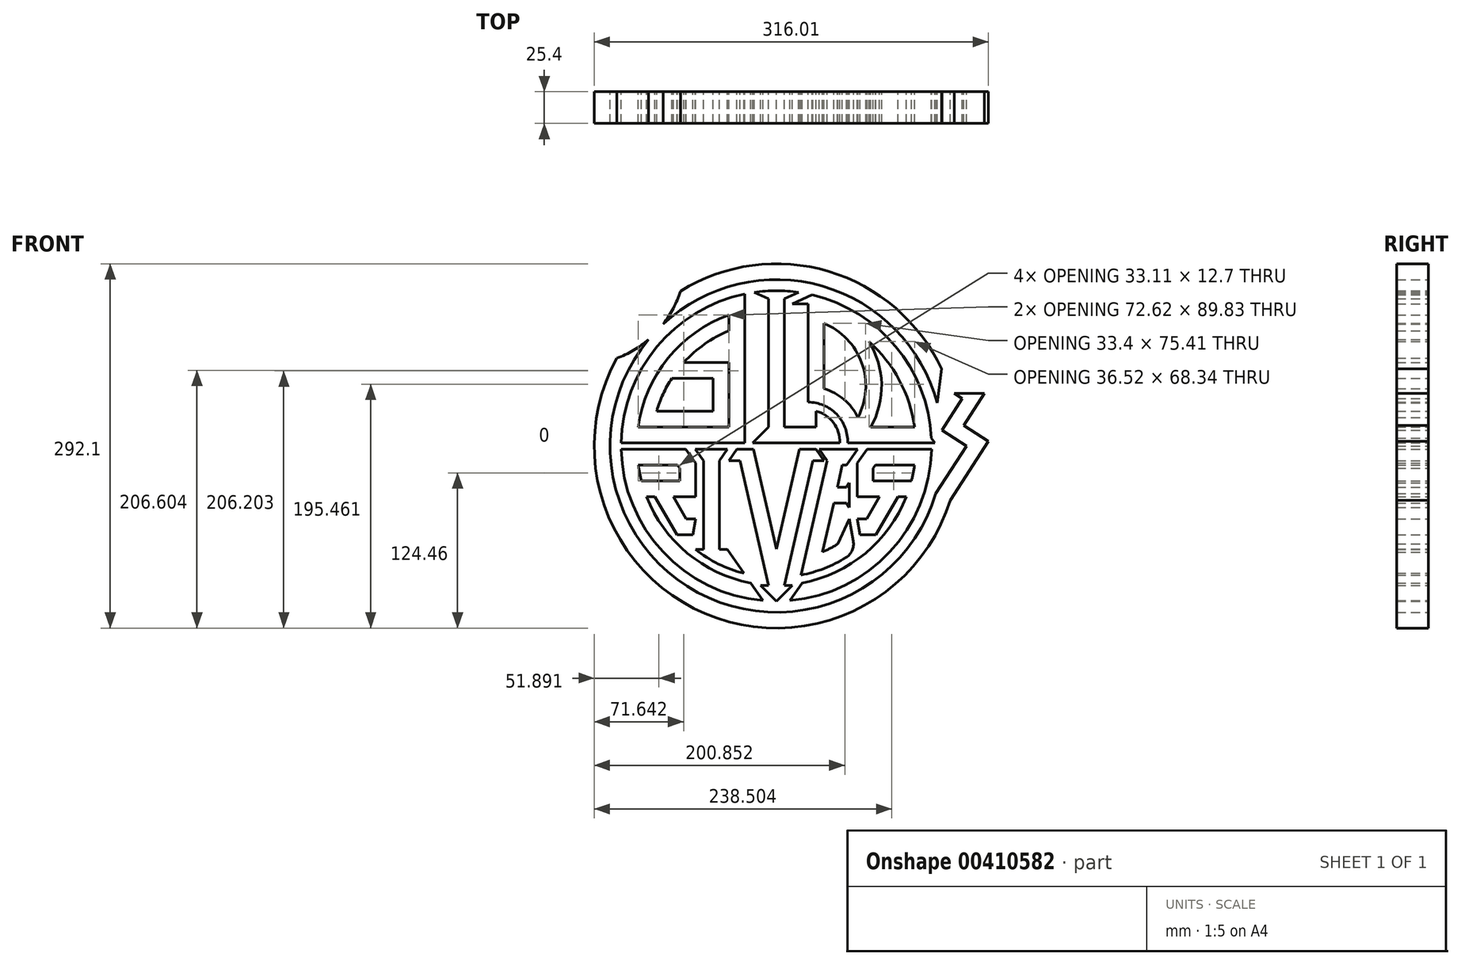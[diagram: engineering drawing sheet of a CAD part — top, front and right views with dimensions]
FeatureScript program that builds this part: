
annotation { "Feature Type Name" : "Feature", "Feature Type Description" : "" }
export const myFeature = defineFeature(function(context is Context, id is Id, definition is map)
    precondition{}
    {
        {
            var Q0;
            Q0=qCreatedBy(makeId("Front.planeOp"),FACE);
            var sketch = newSketch(context, id + "F0", { "sketchPlane" : qUnion([Q0])});
            skCircle(sketch, "E0", {"center": v(0, 0) * mm, "radius": 127 * mm});
            skLineSegment(sketch, "E1", {"start": v(-127, 0) * mm, "end": v(127, 0) * mm, "construction": true});
            skLineSegment(sketch, "E2", {"start": v(0, 127) * mm, "end": v(0, -127) * mm, "construction": true});
            skSolve(sketch);
        }
        {
            var Q0;
            Q0=qCreatedBy(makeId("Front.planeOp"),FACE);
            var sketch = newSketch(context, id + "F1", { "sketchPlane" : qUnion([Q0])});
            skArc(sketch, "E3", {"start": v(-124.43, 2.54) * mm, "mid": v(-95.76, 79.5) * mm, "end": v(-25.4, 121.84) * mm});
            skPoint(sketch, "E4.visualSharp", {"position": v(-124.46, 0) * mm});
            skPoint(sketch, "E5.visualSharp", {"position": v(0, 10.87) * mm});
            skPoint(sketch, "E6.visualSharp", {"position": v(-44.61, 116.2) * mm});
            skLineSegment(sketch, "E7", {"start": v(-25.4, 121.84) * mm, "end": v(-25.4, 2.54) * mm});
            skLineSegment(sketch, "E8", {"start": v(-25.4, 2.54) * mm, "end": v(-124.43, 2.54) * mm});
            skLineSegment(sketch, "E9", {"start": v(-17.78, 123.18) * mm, "end": v(-17.78, 123.18) * mm});
            skLineSegment(sketch, "E10", {"start": v(17.78, 123.18) * mm, "end": v(17.78, 123.18) * mm});
            skArc(sketch, "E11", {"start": v(17.78, 123.18) * mm, "mid": v(0, 124.46) * mm, "end": v(-17.78, 123.18) * mm});
            skPoint(sketch, "E12", {"position": v(0, 124.46) * mm});
            skLineSegment(sketch, "E13", {"start": v(-17.78, 123.18) * mm, "end": v(-6.35, 118.11) * mm});
            skLineSegment(sketch, "E14", {"start": v(-6.35, 118.11) * mm, "end": v(-6.35, 15.24) * mm});
            skLineSegment(sketch, "E15", {"start": v(17.78, 123.18) * mm, "end": v(6.35, 118.11) * mm});
            skLineSegment(sketch, "E16", {"start": v(6.35, 118.11) * mm, "end": v(6.35, 15.24) * mm});
            skLineSegment(sketch, "E17", {"start": v(-6.35, 15.24) * mm, "end": v(-19.05, 2.54) * mm});
            skLineSegment(sketch, "E18", {"start": v(-19.05, 2.54) * mm, "end": v(50.8, 2.54) * mm});
            skLineSegment(sketch, "E19", {"start": v(6.35, 15.24) * mm, "end": v(31.75, 15.24) * mm});
            skLineSegment(sketch, "E20", {"start": v(31.75, 15.24) * mm, "end": v(31.75, 27.94) * mm});
            skArc(sketch, "E21", {"start": v(50.8, 2.54) * mm, "mid": v(45.73, 18.58) * mm, "end": v(31.75, 27.94) * mm});
            skArc(sketch, "E22", {"start": v(-38.1, 105.07) * mm, "mid": v(-86.91, 70.26) * mm, "end": v(-110.72, 15.24) * mm});
            skLineSegment(sketch, "E23", {"start": v(-110.72, 15.24) * mm, "end": v(-38.1, 15.24) * mm});
            skLineSegment(sketch, "E24", {"start": v(-38.1, 15.24) * mm, "end": v(-38.1, 66.97) * mm});
            skLineSegment(sketch, "E25", {"start": v(-38.1, 66.97) * mm, "end": v(-74.15, 66.97) * mm});
            skLineSegment(sketch, "E26", {"start": v(-38.1, 105.07) * mm, "end": v(-38.1, 92.37) * mm});
            skArc(sketch, "E27", {"start": v(-38.1, 92.37) * mm, "mid": v(-57.55, 81.68) * mm, "end": v(-74.15, 66.97) * mm});
            skLineSegment(sketch, "E28.bottom", {"start": v(-50.8, 54.27) * mm, "end": v(-83.9, 54.27) * mm});
            skLineSegment(sketch, "E28.top", {"start": v(-50.8, 27.94) * mm, "end": v(-95.93, 27.94) * mm});
            skLineSegment(sketch, "E28.left", {"start": v(-50.8, 54.27) * mm, "end": v(-50.8, 27.94) * mm});
            skArc(sketch, "E29", {"start": v(-83.9, 54.27) * mm, "mid": v(-90.87, 41.54) * mm, "end": v(-95.93, 27.94) * mm});
            skSolve(sketch);
        }
        {
            var Q0;
            Q0=qCreatedBy(makeId("Front.planeOp"),FACE);
            var sketch = newSketch(context, id + "F2", { "sketchPlane" : qUnion([Q0])});
            skLineSegment(sketch, "E30", {"start": v(57.15, 2.54) * mm, "end": v(126.97, 2.54) * mm});
            skPoint(sketch, "E31.start.orphan", {"position": v(50.8, 46.41) * mm});
            skArc(sketch, "E32", {"start": v(25.4, 35.1) * mm, "mid": v(48.14, 25.51) * mm, "end": v(57.15, 2.54) * mm});
            skLineSegment(sketch, "E33", {"start": v(25.4, 35.1) * mm, "end": v(25.4, 113.98) * mm});
            skLineSegment(sketch, "E34", {"start": v(25.4, 113.98) * mm, "end": v(12.7, 113.98) * mm});
            skLineSegment(sketch, "E35", {"start": v(28.73, 121.1) * mm, "end": v(12.7, 113.98) * mm});
            skLineSegment(sketch, "E36", {"start": v(124.3, 6.35) * mm, "end": v(126.97, 2.54) * mm});
            skArc(sketch, "E37", {"start": v(28.73, 121.1) * mm, "mid": v(95.64, 79.65) * mm, "end": v(124.3, 6.35) * mm});
            skLineSegment(sketch, "E38", {"start": v(38.1, 105.07) * mm, "end": v(38.1, 45.94) * mm});
            skLineSegment(sketch, "E39", {"start": v(68.24, 15.24) * mm, "end": v(110.72, 15.24) * mm});
            skArc(sketch, "E40", {"start": v(38.1, 45.94) * mm, "mid": v(57.13, 34.48) * mm, "end": v(68.24, 15.24) * mm});
            skArc(sketch, "E41", {"start": v(38.1, 105.07) * mm, "mid": v(86.91, 70.26) * mm, "end": v(110.72, 15.24) * mm});
            skPoint(sketch, "E42.start.orphan", {"position": v(86.91, 70.26) * mm});
            skArc(sketch, "E43", {"start": v(68.24, 15.24) * mm, "mid": v(74.84, 67.42) * mm, "end": v(38.1, 105.07) * mm, "construction": true});
            skArc(sketch, "E44.0", {"start": v(75.66, 15.24) * mm, "mid": v(84.32, 49.61) * mm, "end": v(74.2, 83.58) * mm});
            skArc(sketch, "E45.0", {"start": v(65.35, 22.85) * mm, "mid": v(68.41, 66.58) * mm, "end": v(38.1, 98.26) * mm});
            skSolve(sketch);
        }
        {
            var Q0;
            Q0 = qSketchRegion(id + "F1", true);
            extrude(context, id + "F3", {"entities" : qUnion([Q0]), "depth" : 25.4 * mm});
        }
        {
            var Q0;
            Q0=qCreatedBy(makeId("Front.planeOp"),FACE);
            var sketch = newSketch(context, id + "F4", { "sketchPlane" : qUnion([Q0])});
            skLineSegment(sketch, "E46.0", {"start": v(-50.8, 54.27) * mm, "end": v(-83.9, 54.27) * mm});
            skPoint(sketch, "E47.0", {"position": v(-50.8, 27.94) * mm});
            skLineSegment(sketch, "E48.0", {"start": v(-50.8, 54.27) * mm, "end": v(-50.8, 27.94) * mm});
            skLineSegment(sketch, "E49.0", {"start": v(-50.8, 27.94) * mm, "end": v(-95.93, 27.94) * mm});
            skArc(sketch, "E50.0", {"start": v(-83.9, 54.27) * mm, "mid": v(-90.87, 41.54) * mm, "end": v(-95.93, 27.94) * mm});
            skSolve(sketch);
        }
        {
            var Q0;
            Q0 = qSketchRegion(id + "F4", true);
            extrude(context, id + "F5", {"entities" : qUnion([Q0]), "depth" : 25.4 * mm});
        }
        {
            var Q0;
            Q0 = qSketchRegion(id + "F2", true);
            extrude(context, id + "F6", {"entities" : qUnion([Q0]), "depth" : 25.4 * mm});
        }
        {
            var Q0;
            Q0=qCreatedBy(makeId("Front.planeOp"),FACE);
            var sketch = newSketch(context, id + "F7", { "sketchPlane" : qUnion([Q0])});
            skArc(sketch, "E51.0", {"start": v(65.35, 22.85) * mm, "mid": v(68.41, 66.58) * mm, "end": v(38.1, 98.26) * mm});
            skArc(sketch, "E52.0", {"start": v(75.66, 15.24) * mm, "mid": v(84.32, 49.61) * mm, "end": v(74.2, 83.58) * mm});
            skArc(sketch, "E53.0", {"start": v(38.1, 105.07) * mm, "mid": v(57.16, 96.03) * mm, "end": v(74.2, 83.58) * mm});
            skArc(sketch, "E54.0", {"start": v(65.35, 22.85) * mm, "mid": v(66.97, 19.11) * mm, "end": v(68.24, 15.24) * mm});
            skLineSegment(sketch, "E55.0", {"start": v(68.24, 15.24) * mm, "end": v(75.66, 15.24) * mm});
            skLineSegment(sketch, "E56.0", {"start": v(38.1, 105.07) * mm, "end": v(38.1, 98.26) * mm});
            skPoint(sketch, "E57.orphan", {"position": v(38.1, 45.94) * mm});
            skPoint(sketch, "E58.orphan", {"position": v(110.72, 15.24) * mm});
            skSolve(sketch);
        }
        {
            var Q0;
            Q0 = qSketchRegion(id + "F7", true);
            extrude(context, id + "F8", {"entities" : qUnion([Q0]), "operationType" : NewBodyOperationType.ADD, "depth" : 25.4 * mm});
        }
        {
            var Q0;
            Q0=qCreatedBy(makeId("Front.planeOp"),FACE);
            var sketch = newSketch(context, id + "F9", { "sketchPlane" : qUnion([Q0])});
            skLineSegment(sketch, "E59", {"start": v(-31.64, -2.54) * mm, "end": v(-38.1, -11.76) * mm});
            skLineSegment(sketch, "E60", {"start": v(-38.1, -11.76) * mm, "end": v(-29.21, -11.76) * mm});
            skLineSegment(sketch, "E61", {"start": v(-31.64, -2.54) * mm, "end": v(-18.3, -2.54) * mm});
            skLineSegment(sketch, "E62", {"start": v(-18.3, -2.54) * mm, "end": v(0, -82.55) * mm});
            skPoint(sketch, "E63.end.orphan", {"position": v(0, -100.04) * mm});
            skLineSegment(sketch, "E64", {"start": v(-29.21, -11.76) * mm, "end": v(-6.35, -111.76) * mm});
            skLineSegment(sketch, "E65", {"start": v(-6.35, -111.76) * mm, "end": v(-12.7, -111.76) * mm});
            skLineSegment(sketch, "E66", {"start": v(-12.7, -111.76) * mm, "end": v(0, -124.46) * mm});
            skLineSegment(sketch, "E67.MirrorCS", {"start": v(12.7, -111.76) * mm, "end": v(0, -124.46) * mm});
            skLineSegment(sketch, "E68.MirrorCS", {"start": v(29.21, -11.76) * mm, "end": v(6.35, -111.76) * mm});
            skLineSegment(sketch, "E69.MirrorCS", {"start": v(6.35, -111.76) * mm, "end": v(12.7, -111.76) * mm});
            skLineSegment(sketch, "E70.MirrorCS", {"start": v(18.3, -2.54) * mm, "end": v(0, -82.55) * mm});
            skLineSegment(sketch, "E71.MirrorCS", {"start": v(31.64, -2.54) * mm, "end": v(38.1, -11.76) * mm});
            skLineSegment(sketch, "E72.MirrorCS", {"start": v(38.1, -11.76) * mm, "end": v(29.21, -11.76) * mm});
            skLineSegment(sketch, "E73", {"start": v(18.3, -2.54) * mm, "end": v(31.64, -2.54) * mm});
            skLineSegment(sketch, "E74", {"start": v(-65.01, -2.54) * mm, "end": v(-39.4, -2.54) * mm});
            skLineSegment(sketch, "E75", {"start": v(-39.4, -2.54) * mm, "end": v(-45.85, -11.76) * mm});
            skLineSegment(sketch, "E76", {"start": v(-45.85, -11.76) * mm, "end": v(-45.85, -83.06) * mm});
            skLineSegment(sketch, "E77", {"start": v(-65.01, -2.54) * mm, "end": v(-58.55, -11.76) * mm});
            skLineSegment(sketch, "E78", {"start": v(-58.55, -11.76) * mm, "end": v(-58.55, -83.06) * mm});
            skLineSegment(sketch, "E79", {"start": v(-26.16, -102.11) * mm, "end": v(-39.5, -83.06) * mm});
            skLineSegment(sketch, "E80", {"start": v(-45.85, -83.06) * mm, "end": v(-39.5, -83.06) * mm});
            skLineSegment(sketch, "E81", {"start": v(-58.55, -83.06) * mm, "end": v(-64.9, -83.06) * mm});
            skArc(sketch, "E82", {"start": v(-64.9, -83.06) * mm, "mid": v(-46.52, -94.6) * mm, "end": v(-26.16, -102.11) * mm});
            skLineSegment(sketch, "E83", {"start": v(-124.43, -2.54) * mm, "end": v(-72.76, -2.54) * mm});
            skLineSegment(sketch, "E84", {"start": v(-72.76, -2.54) * mm, "end": v(-64.9, -13.77) * mm});
            skLineSegment(sketch, "E85", {"start": v(-64.9, -13.77) * mm, "end": v(-64.9, -40.64) * mm});
            skLineSegment(sketch, "E86", {"start": v(-64.9, -40.64) * mm, "end": v(-82.68, -40.64) * mm});
            skLineSegment(sketch, "E87", {"start": v(-82.68, -40.64) * mm, "end": v(-72.42, -58.42) * mm});
            skLineSegment(sketch, "E88", {"start": v(-72.42, -58.42) * mm, "end": v(-64.9, -58.42) * mm});
            skLineSegment(sketch, "E89", {"start": v(-64.9, -58.42) * mm, "end": v(-67.14, -71.12) * mm});
            skLineSegment(sketch, "E90", {"start": v(-67.14, -71.12) * mm, "end": v(-79.75, -71.12) * mm});
            skLineSegment(sketch, "E91", {"start": v(-79.75, -71.12) * mm, "end": v(-97.35, -40.64) * mm});
            skArc(sketch, "E92", {"start": v(-124.43, -2.54) * mm, "mid": v(-90.9, -85.02) * mm, "end": v(-10.84, -123.99) * mm});
            skArc(sketch, "E93", {"start": v(-104.1, -40.64) * mm, "mid": v(-71.38, -86) * mm, "end": v(-20.77, -109.81) * mm});
            skLineSegment(sketch, "E94", {"start": v(-97.35, -40.64) * mm, "end": v(-104.1, -40.64) * mm});
            skLineSegment(sketch, "E95", {"start": v(-20.77, -109.81) * mm, "end": v(-10.84, -123.99) * mm});
            skLineSegment(sketch, "E96", {"start": v(-20.77, -109.81) * mm, "end": v(-26.16, -102.11) * mm, "construction": true});
            skArc(sketch, "E97.MirrorCS", {"start": v(124.43, -2.54) * mm, "mid": v(90.9, -85.02) * mm, "end": v(10.84, -123.99) * mm});
            skLineSegment(sketch, "E98.MirrorCS", {"start": v(20.77, -109.81) * mm, "end": v(10.84, -123.99) * mm});
            skArc(sketch, "E99.MirrorCS", {"start": v(104.1, -40.64) * mm, "mid": v(71.38, -86) * mm, "end": v(20.77, -109.81) * mm});
            skLineSegment(sketch, "E100.MirrorCS", {"start": v(124.43, -2.54) * mm, "end": v(72.76, -2.54) * mm});
            skLineSegment(sketch, "E101.MirrorCS", {"start": v(97.35, -40.64) * mm, "end": v(104.1, -40.64) * mm});
            skLineSegment(sketch, "E102.MirrorCS", {"start": v(79.75, -71.12) * mm, "end": v(97.35, -40.64) * mm});
            skLineSegment(sketch, "E103.MirrorCS", {"start": v(67.14, -71.12) * mm, "end": v(79.75, -71.12) * mm});
            skLineSegment(sketch, "E104.MirrorCS", {"start": v(82.68, -40.64) * mm, "end": v(72.42, -58.42) * mm});
            skLineSegment(sketch, "E105.MirrorCS", {"start": v(72.42, -58.42) * mm, "end": v(64.9, -58.42) * mm});
            skLineSegment(sketch, "E106.MirrorCS", {"start": v(64.9, -58.42) * mm, "end": v(67.14, -71.12) * mm});
            skLineSegment(sketch, "E107.MirrorCS", {"start": v(64.9, -40.64) * mm, "end": v(82.68, -40.64) * mm});
            skLineSegment(sketch, "E108.MirrorCS", {"start": v(64.9, -13.77) * mm, "end": v(64.9, -40.64) * mm});
            skLineSegment(sketch, "E109.MirrorCS", {"start": v(72.76, -2.54) * mm, "end": v(64.9, -13.77) * mm});
            skSolve(sketch);
        }
        {
            var Q0;
            Q0 = qSketchRegion(id + "F9", true);
            extrude(context, id + "F10", {"entities" : qUnion([Q0]), "depth" : 25.4 * mm});
        }
        {
            var Q0;
            Q0=qCreatedBy(makeId("Front.planeOp"),FACE);
            var sketch = newSketch(context, id + "F11", { "sketchPlane" : qUnion([Q0])});
            skLineSegment(sketch, "E110.0", {"start": v(-77.6, -27.94) * mm, "end": v(-108.21, -27.94) * mm});
            skLineSegment(sketch, "E110.2", {"start": v(-110.72, -15.24) * mm, "end": v(-79.37, -15.24) * mm});
            skLineSegment(sketch, "E110.3", {"start": v(-79.37, -15.24) * mm, "end": v(-77.6, -17.77) * mm});
            skLineSegment(sketch, "E110.4", {"start": v(-77.6, -17.77) * mm, "end": v(-77.6, -27.94) * mm});
            skArc(sketch, "E111", {"start": v(-108.21, -27.94) * mm, "mid": v(-109.65, -21.63) * mm, "end": v(-110.72, -15.24) * mm});
            skArc(sketch, "E112", {"start": v(-108.21, -27.94) * mm, "mid": v(-106.35, -34.35) * mm, "end": v(-104.1, -40.64) * mm, "construction": true});
            skLineSegment(sketch, "E113.MirrorCS", {"start": v(77.6, -27.94) * mm, "end": v(108.21, -27.94) * mm});
            skLineSegment(sketch, "E114.MirrorCS", {"start": v(77.6, -17.77) * mm, "end": v(77.6, -27.94) * mm});
            skLineSegment(sketch, "E115.MirrorCS", {"start": v(79.37, -15.24) * mm, "end": v(77.6, -17.77) * mm});
            skLineSegment(sketch, "E116.MirrorCS", {"start": v(110.72, -15.24) * mm, "end": v(79.37, -15.24) * mm});
            skArc(sketch, "E117.MirrorCS", {"start": v(108.21, -27.94) * mm, "mid": v(109.65, -21.63) * mm, "end": v(110.72, -15.24) * mm});
            skSolve(sketch);
        }
        {
            var Q0;
            Q0 = qSketchRegion(id + "F11", true);
            extrude(context, id + "F12", {"entities" : qUnion([Q0]), "operationType" : NewBodyOperationType.REMOVE, "endBound" : BoundingType.THROUGH_ALL, "depth" : 25.4 * mm});
        }
        {
            var Q0;
            Q0=qCreatedBy(makeId("Front.planeOp"),FACE);
            var sketch = newSketch(context, id + "F13", { "sketchPlane" : qUnion([Q0])});
            skLineSegment(sketch, "E118", {"start": v(40.64, -11.76) * mm, "end": v(19.65, -103.56) * mm});
            skLineSegment(sketch, "E119", {"start": v(34.18, -2.54) * mm, "end": v(65.01, -2.54) * mm});
            skLineSegment(sketch, "E120", {"start": v(65.01, -2.54) * mm, "end": v(56.12, -15.24) * mm});
            skLineSegment(sketch, "E121", {"start": v(56.12, -15.24) * mm, "end": v(52.87, -15.24) * mm});
            skLineSegment(sketch, "E122", {"start": v(52.87, -15.24) * mm, "end": v(48.8, -33.02) * mm});
            skLineSegment(sketch, "E123", {"start": v(48.8, -33.02) * mm, "end": v(56.12, -33.02) * mm});
            skLineSegment(sketch, "E124", {"start": v(56.12, -45.72) * mm, "end": v(45.9, -45.72) * mm});
            skLineSegment(sketch, "E125", {"start": v(45.9, -45.72) * mm, "end": v(36.92, -85.04) * mm});
            skLineSegment(sketch, "E126", {"start": v(48.8, -33.02) * mm, "end": v(45.9, -45.72) * mm, "construction": true});
            skArc(sketch, "E127", {"start": v(19.65, -103.56) * mm, "mid": v(38.41, -98.16) * mm, "end": v(55.85, -89.4) * mm});
            skArc(sketch, "E128", {"start": v(55.85, -89.4) * mm, "mid": v(60.72, -83.8) * mm, "end": v(61.63, -76.42) * mm});
            skArc(sketch, "E129", {"start": v(-20.77, -109.81) * mm, "mid": v(46.56, -101.6) * mm, "end": v(96.73, -55.97) * mm, "construction": true});
            skLineSegment(sketch, "E130", {"start": v(61.63, -76.42) * mm, "end": v(56.42, -46.9) * mm, "construction": true});
            skPoint(sketch, "E131.end.orphan", {"position": v(65.01, -20.32) * mm});
            skLineSegment(sketch, "E132", {"start": v(34.18, -2.54) * mm, "end": v(40.64, -11.76) * mm});
            skLineSegment(sketch, "E133", {"start": v(56.12, -33.02) * mm, "end": v(58.55, -29.54) * mm});
            skLineSegment(sketch, "E134", {"start": v(58.55, -29.54) * mm, "end": v(58.55, -49.2) * mm});
            skLineSegment(sketch, "E135", {"start": v(58.55, -49.2) * mm, "end": v(56.12, -45.72) * mm});
            skArc(sketch, "E136.0", {"start": v(36.92, -85.04) * mm, "mid": v(43.14, -82.06) * mm, "end": v(49.12, -78.63) * mm});
            skLineSegment(sketch, "E137", {"start": v(49.12, -78.63) * mm, "end": v(58.45, -58.42) * mm});
            skLineSegment(sketch, "E138", {"start": v(58.45, -58.42) * mm, "end": v(61.63, -76.42) * mm});
            skSolve(sketch);
        }
        {
            var Q0;
            Q0 = qSketchRegion(id + "F13", true);
            extrude(context, id + "F14", {"entities" : qUnion([Q0]), "depth" : 25.4 * mm});
        }
        {
            var Q0;
            Q0=qCreatedBy(makeId("Front.planeOp"),FACE);
            var sketch = newSketch(context, id + "F15", { "sketchPlane" : qUnion([Q0])});
            skLineSegment(sketch, "E139", {"start": v(149.05, 37.94) * mm, "end": v(132.74, 12.7) * mm});
            skLineSegment(sketch, "E140", {"start": v(132.74, 12.7) * mm, "end": v(152.4, 0) * mm});
            skCircle(sketch, "E141.0", {"center": v(0, 0) * mm, "radius": 133.35 * mm, "construction": true});
            skLineSegment(sketch, "E142", {"start": v(149.05, 37.94) * mm, "end": v(142.65, 42.08) * mm});
            skLineSegment(sketch, "E143", {"start": v(142.65, 42.08) * mm, "end": v(166.84, 42.08) * mm});
            skLineSegment(sketch, "E144", {"start": v(166.84, 42.08) * mm, "end": v(150.3, 16.48) * mm});
            skLineSegment(sketch, "E145", {"start": v(150.3, 16.48) * mm, "end": v(169.96, 3.78) * mm});
            skLineSegment(sketch, "E146", {"start": v(169.96, 3.78) * mm, "end": v(139.43, -43.48) * mm});
            skLineSegment(sketch, "E147", {"start": v(152.4, 0) * mm, "end": v(127.8, -38.08) * mm});
            skPoint(sketch, "E148.end.orphan", {"position": v(245.8, 0) * mm});
            skArc(sketch, "E149", {"start": v(127.8, -38.08) * mm, "mid": v(-133.34, 1.85) * mm, "end": v(128.8, 34.51) * mm});
            skArc(sketch, "E150", {"start": v(139.43, -43.48) * mm, "mid": v(-145.72, -9.78) * mm, "end": v(132.37, 61.72) * mm});
            skLineSegment(sketch, "E151", {"start": v(128.8, 34.51) * mm, "end": v(0, 0) * mm, "construction": true});
            skLineSegment(sketch, "E152", {"start": v(132.37, 61.72) * mm, "end": v(128.8, 34.51) * mm});
            skLineSegment(sketch, "E153", {"start": v(132.37, 61.72) * mm, "end": v(0, 0) * mm, "construction": true});
            skSolve(sketch);
        }
        {
            var Q0;
            Q0 = qSketchRegion(id + "F15", true);
            extrude(context, id + "F16", {"entities" : qUnion([Q0]), "depth" : 25.4 * mm});
        }
        {
            var Q0;
            Q0=qCreatedBy(makeId("Front.planeOp"),FACE);
            var sketch = newSketch(context, id + "F17", { "sketchPlane" : qUnion([Q0])});
            skArc(sketch, "E154", {"start": v(-145.11, 113.37) * mm, "mid": v(-138.92, 120.88) * mm, "end": v(-132.34, 128.05) * mm});
            skLineSegment(sketch, "E155", {"start": v(-132.34, 128.05) * mm, "end": v(-138.73, 134.24) * mm});
            skLineSegment(sketch, "E156", {"start": v(-145.11, 113.37) * mm, "end": v(-140.1, 109.46) * mm});
            skArc(sketch, "E157.0", {"start": v(-140.1, 109.46) * mm, "mid": v(-134.13, 116.71) * mm, "end": v(-127.77, 123.64) * mm});
            skLineSegment(sketch, "E158", {"start": v(0, 0) * mm, "end": v(-136.5, 136.5) * mm, "construction": true});
            skArc(sketch, "E159", {"start": v(-138.73, 134.24) * mm, "mid": v(-136.5, 136.5) * mm, "end": v(-134.24, 138.73) * mm, "construction": true});
            skLineSegment(sketch, "E160", {"start": v(-127.77, 123.64) * mm, "end": v(-120.47, 116.57) * mm});
            skLineSegment(sketch, "E161", {"start": v(-132.34, 128.05) * mm, "end": v(-127.77, 123.64) * mm, "construction": true});
            skArc(sketch, "E162", {"start": v(-120.47, 116.57) * mm, "mid": v(-124.52, 112.24) * mm, "end": v(-128.42, 107.76) * mm});
            skLineSegment(sketch, "E163", {"start": v(-128.42, 107.76) * mm, "end": v(-113.83, 95.51) * mm});
            skArc(sketch, "E164.0", {"start": v(-105.07, 105.07) * mm, "mid": v(-109.55, 100.39) * mm, "end": v(-113.83, 95.51) * mm});
            skArc(sketch, "E165", {"start": v(-136.5, 136.5) * mm, "mid": v(-137.62, 135.37) * mm, "end": v(-138.73, 134.24) * mm});
            skLineSegment(sketch, "E166", {"start": v(-136.5, 136.5) * mm, "end": v(-114.05, 114.05) * mm});
            skArc(sketch, "E167.0", {"start": v(-109.56, 109.56) * mm, "mid": v(-112.06, 107) * mm, "end": v(-114.5, 104.37) * mm});
            skLineSegment(sketch, "E167.1", {"start": v(-119.38, 108.46) * mm, "end": v(-114.5, 104.37) * mm});
            skArc(sketch, "E167.2", {"start": v(-114.05, 114.05) * mm, "mid": v(-116.75, 111.29) * mm, "end": v(-119.38, 108.46) * mm});
            skLineSegment(sketch, "E168", {"start": v(-109.56, 109.56) * mm, "end": v(-105.07, 105.07) * mm});
            skSolve(sketch);
        }
        {
            var Q0;
            Q0 = qSketchRegion(id + "F17", true);
            extrude(context, id + "F18", {"entities" : qUnion([Q0]), "depth" : 25.4 * mm});
        }
        {
            var Q0;
            Q0=makeQuery(id+"F18.opExtrude","SWEPT_BODY",BODY,{"disambiguationData":[OSD([sQuery(id+"F17.wireOp",EDGE,"E154"),sQuery(id+"F17.wireOp",EDGE,"E155"),sQuery(id+"F17.wireOp",EDGE,"E156"),sQuery(id+"F17.wireOp",EDGE,"E157.0"),sQuery(id+"F17.wireOp",EDGE,"E160"),sQuery(id+"F17.wireOp",EDGE,"E162"),sQuery(id+"F17.wireOp",EDGE,"E163"),sQuery(id+"F17.wireOp",EDGE,"E164.0"),sQuery(id+"F17.wireOp",EDGE,"E165"),sQuery(id+"F17.wireOp",EDGE,"E166"),sQuery(id+"F17.wireOp",EDGE,"E167.0"),sQuery(id+"F17.wireOp",EDGE,"E167.1"),sQuery(id+"F17.wireOp",EDGE,"E167.2"),sQuery(id+"F17.wireOp",EDGE,"E168")])]});
            var Q1;
            Q1=makeQuery(id+"F18.opExtrude","SWEPT_FACE",FACE,{"disambiguationData":[OSD([sQuery(id+"F17.wireOp",EDGE,"E166")])]});
            mirror(context, id + "F19", {"operationType" : NewBodyOperationType.ADD, "entities" : qUnion([Q0]), "mirrorPlane" : qUnion([Q1])});
        }
        {
            var Q0;
            Q0=qCreatedBy(makeId("Front.planeOp"),FACE);
            var sketch = newSketch(context, id + "F20", { "sketchPlane" : qUnion([Q0])});
            skCircle(sketch, "E169", {"center": v(-157.5, 149.47) * mm, "radius": 84.5 * mm});
            skSolve(sketch);
        }
        {
            var Q0;
            Q0 = qSketchRegion(id + "F20", true);
            extrude(context, id + "F21", {"entities" : qUnion([Q0]), "operationType" : NewBodyOperationType.REMOVE, "depth" : 25.4 * mm});
        }
    });
